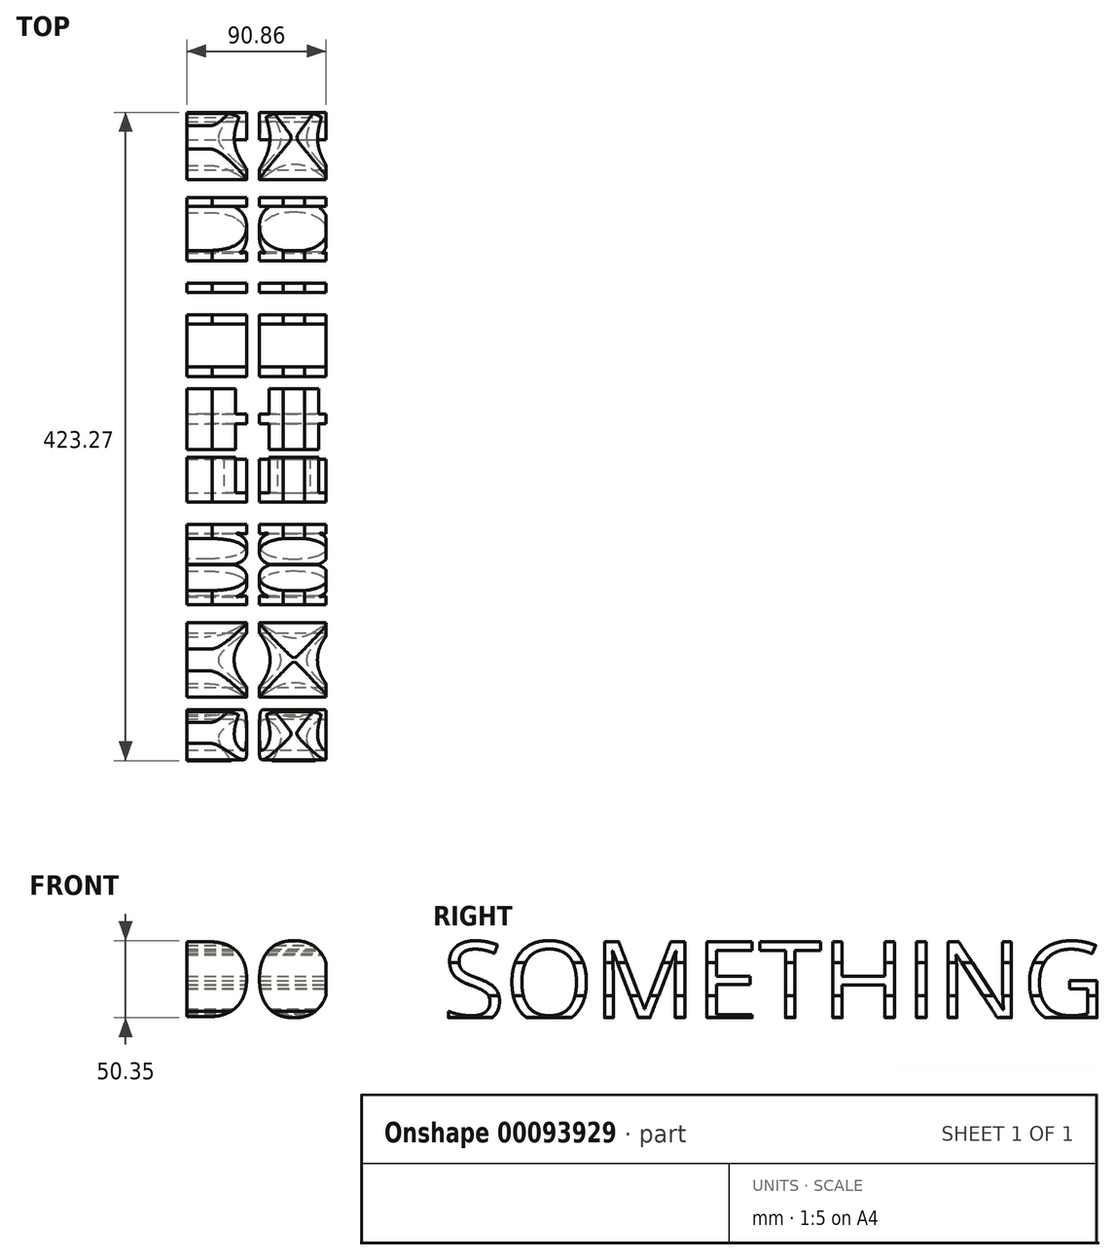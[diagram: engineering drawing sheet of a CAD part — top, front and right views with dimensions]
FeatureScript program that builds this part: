
annotation { "Feature Type Name" : "Feature", "Feature Type Description" : "" }
export const myFeature = defineFeature(function(context is Context, id is Id, definition is map)
    precondition{}
    {
        {
            var Q0;
            Q0=qCreatedBy(makeId("Front.planeOp"),FACE);
            var sketch = newSketch(context, id + "F0", { "sketchPlane" : qUnion([Q0])});
            skText(sketch, "E0", { "text": "DO", "fontName": "OpenSans-Regular.ttf"});
            skLineSegment(sketch, "E1.bottom", {"start": v(-40.2, 28.42) * mm, "end": v(71.25, 28.42) * mm});
            skLineSegment(sketch, "E1.top", {"start": v(-40.2, -37.44) * mm, "end": v(71.25, -37.44) * mm});
            skLineSegment(sketch, "E1.left", {"start": v(-40.2, 28.42) * mm, "end": v(-40.2, -37.44) * mm});
            skLineSegment(sketch, "E1.right", {"start": v(71.25, 28.42) * mm, "end": v(71.25, -37.44) * mm});
            const initialGuessF0  = {"E0": [-0.0417, -0.02892, 1, 0, 0.04933]};
            skSetInitialGuess(sketch, initialGuessF0);
            skSolve(sketch);
        }
        {
            var Q0;
            Q0=qCreatedBy(makeId("Right.planeOp"),FACE);
            var sketch = newSketch(context, id + "F1", { "sketchPlane" : qUnion([Q0])});
            skText(sketch, "E2", { "text": "SOMETHING\n", "fontName": "OpenSans-Regular.ttf"});
            const initialGuessF1  = {"E2": [-0.21355, -0.03293, 1, 0, 0.05334]};
            skSetInitialGuess(sketch, initialGuessF1);
            skSolve(sketch);
        }
        {
            var Q0;
            Q0 = qSketchRegion(id + "F1", true);
            extrude(context, id + "F2", {"entities" : qUnion([Q0]), "oppositeDirection" : true, "depth" : 35.56 * mm, "hasSecondDirection" : true, "secondDirectionOppositeDirection" : false, "secondDirectionDepth" : 55.88 * mm});
        }
        {
            var Q0;
            Q0=makeQuery(id+"F0.imprint","IMPRINT",FACE,{"disambiguationData":[TD([[makeQuery(id+"F0.imprint","IMPRINT",EDGE,{"derivedFrom":sQuery(id+"F0.wireOp",EDGE,"E0.sketch_text.stroke-0")}),1.0]])]});
            extrude(context, id + "F3", {"entities" : qUnion([Q0]), "operationType" : NewBodyOperationType.REMOVE, "oppositeDirection" : true, "depth" : 254 * mm, "hasSecondDirection" : true, "secondDirectionOppositeDirection" : false, "secondDirectionDepth" : 254 * mm});
        }
    });
